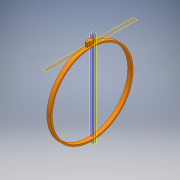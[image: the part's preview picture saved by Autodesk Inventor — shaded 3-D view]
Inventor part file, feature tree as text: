
AUTODESK INVENTOR PART (.ipt)
format: ipt  version: 2018 (Build 220112000, 112)  size: 187,392 bytes
history: native  units: mm
features: extrude x6, sketch x6, plane x5, projected_geometry x3, mirror x2
ambient origin geometry x8: Origin, YZ Plane, XZ Plane, XY Plane, X Axis, Y Axis, Z Axis, Center Point
bodies: Solid1 (feature_tree)
feature tree (22):
  extrude  "Extrusion1"  Depth=204.0mm
  plane  "Work Plane1"
  extrude  "Extrusion2"  Depth=10.0mm
  plane  "Work Plane2"
  extrude  "Extrusion3"  Depth=6.0mm
  mirror  "Mirror1"
  plane  "Work Plane3"
  extrude  "Extrusion4"  Depth=5.0mm TaperAngle=0.0deg
  extrude  "Extrusion5"  Depth=5.0mm
  plane  "Work Plane5"
  extrude  "Extrusion6"  Depth=10.0mm
  mirror  "Mirror2"
  sketch  "Sketch1"  dims[d0=212.0mm d1=204.0mm]
  sketch  "Sketch2"  dims[d2=10.0mm d3=0.0mm d4=4.0mm]
  projected_geometry  "Projected Loop1"
  sketch  "Sketch3"  dims[d5=227.25mm d6=0.0mm d7=6.0mm]
  sketch  "Sketch4"  dims[d8=5.0mm d9=0.0mm d10=1.0mm d11=0.0mm]
  sketch  "Sketch5"  dims[d12=10.0mm d13=0.0mm d14=5.0mm]
  projected_geometry  "Projected Loop2"
  plane  "Work Plane4"
  sketch  "Sketch6"  dims[d15=12.0mm d16=2.5mm d17=2.5mm d18=12.0mm d19=10.0mm d20=0.0mm]
  projected_geometry  "Projected Loop3"
